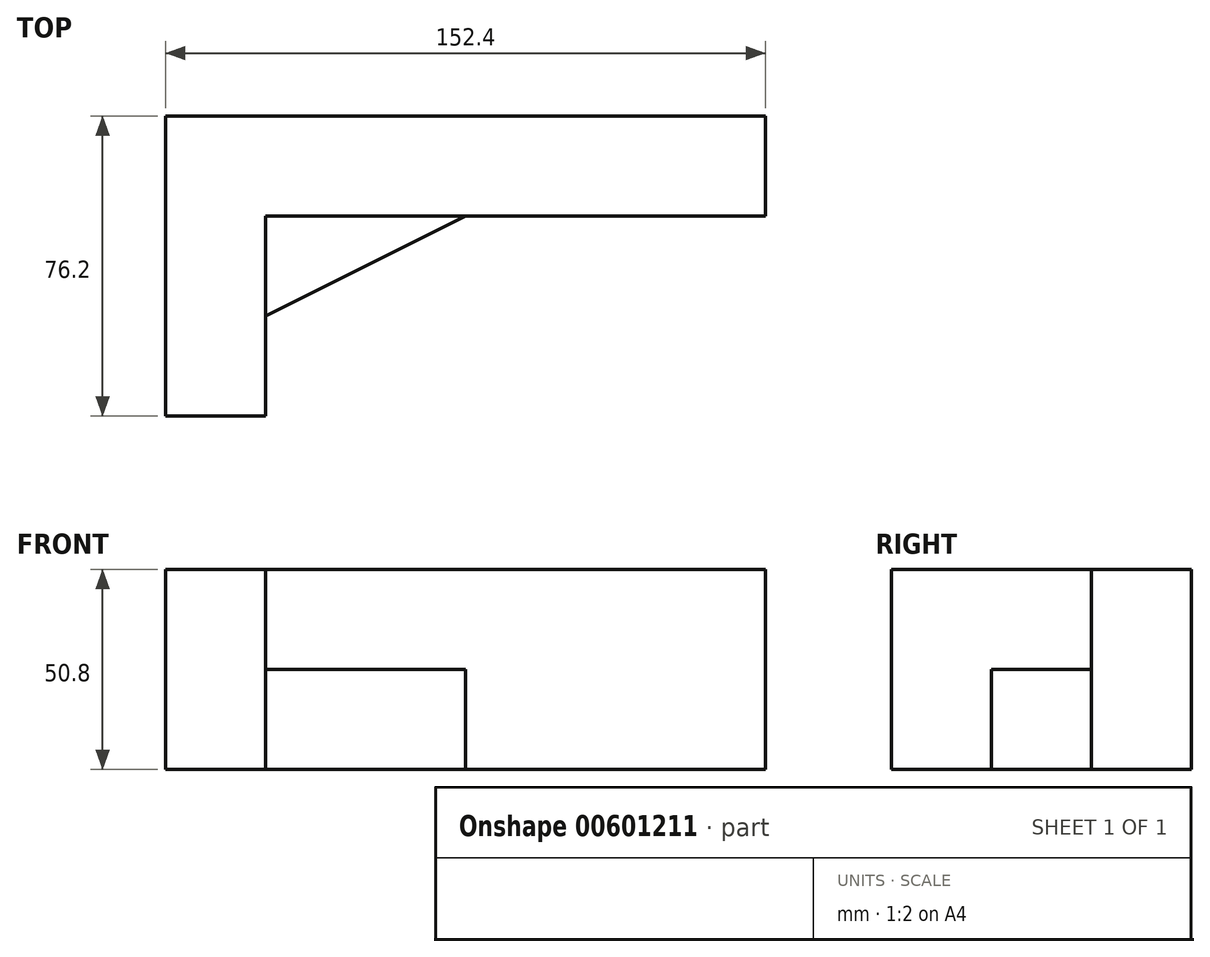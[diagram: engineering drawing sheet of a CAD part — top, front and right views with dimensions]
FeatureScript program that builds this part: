
annotation { "Feature Type Name" : "Feature", "Feature Type Description" : "" }
export const myFeature = defineFeature(function(context is Context, id is Id, definition is map)
    precondition{}
    {
        {
            var Q0;
            Q0=qCreatedBy(makeId("Front.planeOp"),FACE);
            var sketch = newSketch(context, id + "F0", { "sketchPlane" : qUnion([Q0])});
            skLineSegment(sketch, "E0", {"start": v(0, 0) * mm, "end": v(0, 50.8) * mm});
            skLineSegment(sketch, "E1", {"start": v(0, 50.8) * mm, "end": v(25.4, 50.8) * mm});
            skLineSegment(sketch, "E2", {"start": v(25.4, 50.8) * mm, "end": v(25.4, 0) * mm});
            skLineSegment(sketch, "E3", {"start": v(25.4, 0) * mm, "end": v(0, 0) * mm});
            skSolve(sketch);
        }
        {
            var Q0;
            Q0=makeQuery(id+"F0.imprint","IMPRINT",FACE,{"disambiguationData":[TD([[makeQuery(id+"F0.imprint","IMPRINT",EDGE,{"derivedFrom":sQuery(id+"F0.wireOp",EDGE,"E0")}),-1.0]])]});
            extrude(context, id + "F1", {"entities" : qUnion([Q0]), "depth" : 76.2 * mm, "offsetDistance" : 25.4 * mm});
        }
        {
            var Q0;
            Q0=makeQuery(id+"F1.opExtrude","SWEPT_FACE",FACE,{"disambiguationData":[OSD([sQuery(id+"F0.wireOp",EDGE,"E2")])]});
            var sketch = newSketch(context, id + "F2", { "sketchPlane" : qUnion([Q0])});
            skLineSegment(sketch, "E4", {"start": v(0, 50.8) * mm, "end": v(-25.4, 50.8) * mm});
            skLineSegment(sketch, "E5", {"start": v(-25.4, 50.8) * mm, "end": v(-25.4, 0) * mm});
            skSolve(sketch);
        }
        {
            var Q0;
            Q0 = qSketchRegion(id + "F2", true);
            var Q1;
            Q1=makeQuery(id+"F2.imprint","IMPRINT",FACE,{"disambiguationData":[TD([[makeQuery(id+"F2.imprint","IMPRINT",EDGE,{"derivedFrom":sQuery(id+"F2.wireOp",EDGE,"E4")}),-1.0]])]});
            extrude(context, id + "F3", {"entities" : qUnion([Q0, Q1]), "operationType" : NewBodyOperationType.ADD, "depth" : 127 * mm, "offsetDistance" : 25.4 * mm});
        }
        {
            var Q0;
            {var subQ0=sQuery(id+"F0.wireOp",EDGE,"E3");Q0=makeQuery(id+"F3.boolean.opBoolean","MERGE",FACE,{"derivedFrom":[makeQuery(id+"F1.opExtrude","SWEPT_FACE",FACE,{"disambiguationData":[OSD([subQ0])]}),makeQuery(id+"F3.opExtrude","SWEPT_FACE",FACE,{"disambiguationData":[OSD([sQuery(id+"F0.wireOp",EDGE,"E2"),subQ0])]})]});}
            var sketch = newSketch(context, id + "F4", { "sketchPlane" : qUnion([Q0])});
            skLineSegment(sketch, "E6", {"start": v(25.4, 25.4) * mm, "end": v(76.2, 25.4) * mm});
            skLineSegment(sketch, "E7", {"start": v(76.2, 25.4) * mm, "end": v(25.4, 50.8) * mm});
            skSolve(sketch);
        }
        {
            var Q0;
            Q0 = qSketchRegion(id + "F4", true);
            var Q1;
            {var subQ0=sQuery(id+"F4.wireOp",EDGE,"E6");Q1=makeQuery(id+"F4.imprint","IMPRINT",FACE,{"disambiguationData":[TD([[makeQuery(id+"F4.imprint","IMPRINT",EDGE,{"derivedFrom":subQ0}),-1.0]])]});}
            extrude(context, id + "F5", {"entities" : qUnion([Q0, Q1]), "operationType" : NewBodyOperationType.ADD, "oppositeDirection" : true, "depth" : 25.4 * mm, "offsetDistance" : 25.4 * mm});
        }
    });
